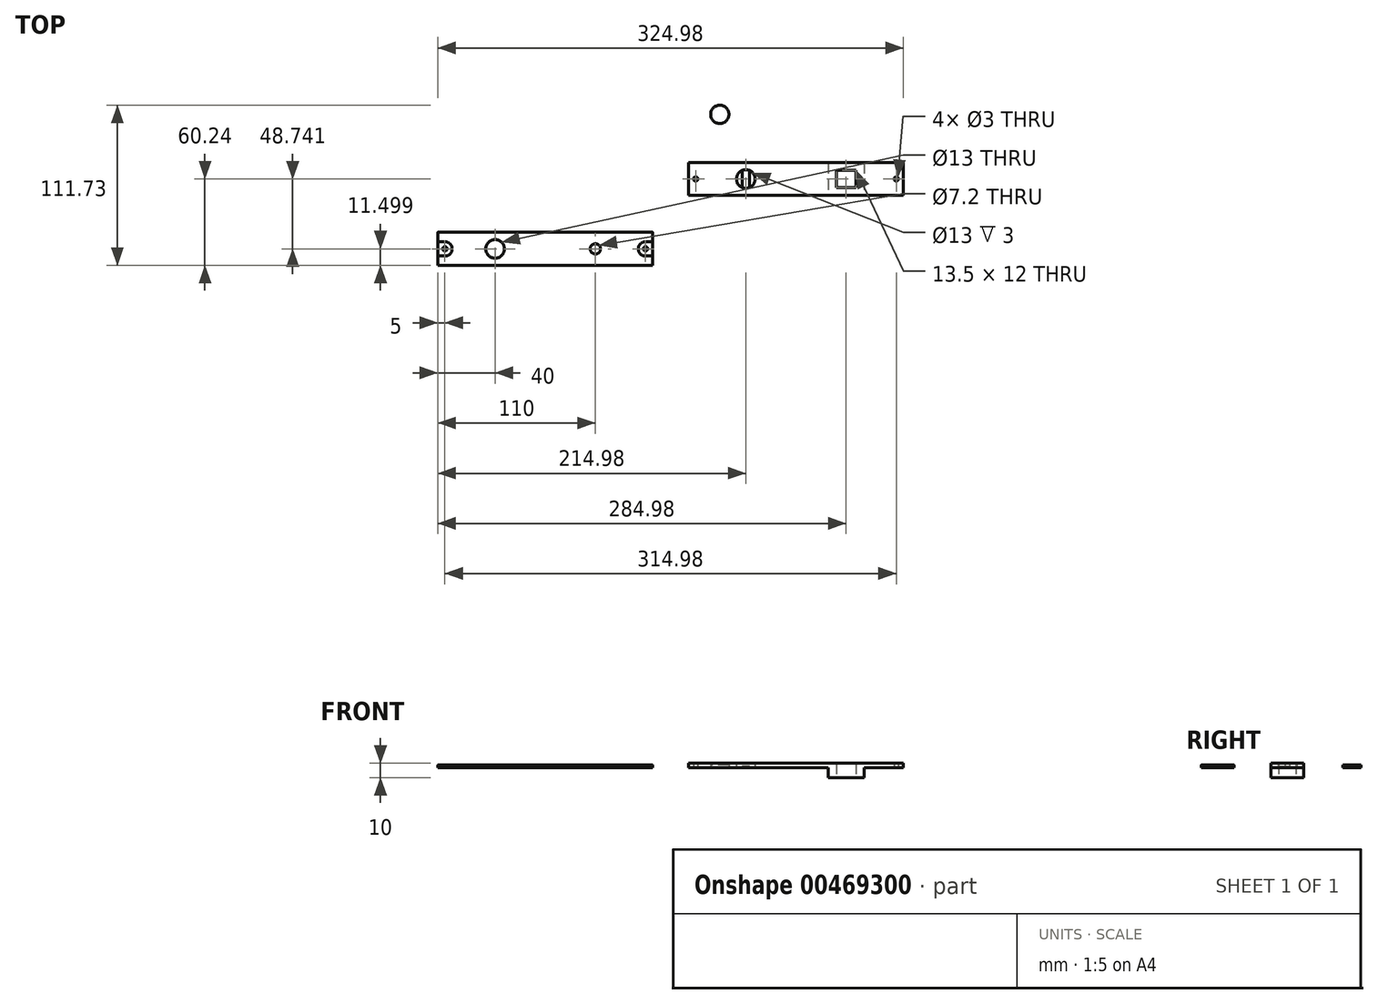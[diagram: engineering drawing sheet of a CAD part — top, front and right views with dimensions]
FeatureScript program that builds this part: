
annotation { "Feature Type Name" : "Feature", "Feature Type Description" : "" }
export const myFeature = defineFeature(function(context is Context, id is Id, definition is map)
    precondition{}
    {
        {
            var Q0;
            Q0=qCreatedBy(makeId("Top.planeOp"),FACE);
            var sketch = newSketch(context, id + "F0", { "sketchPlane" : qUnion([Q0])});
            skLineSegment(sketch, "E0.bottom", {"start": v(75, -11.5) * mm, "end": v(-75, -11.5) * mm});
            skLineSegment(sketch, "E0.top", {"start": v(75, 11.5) * mm, "end": v(-75, 11.5) * mm});
            skLineSegment(sketch, "E0.left", {"start": v(75, -11.5) * mm, "end": v(75, 11.5) * mm});
            skLineSegment(sketch, "E0.right", {"start": v(-75, -11.5) * mm, "end": v(-75, 11.5) * mm});
            skPoint(sketch, "E0.middle", {"position": v(0, 0) * mm});
            skCircle(sketch, "E1", {"center": v(-35, 0) * mm, "radius": 6.5 * mm});
            skLineSegment(sketch, "E2.bottom", {"start": v(-75, 11.5) * mm, "end": v(-65, 11.5) * mm, "construction": true});
            skLineSegment(sketch, "E2.top", {"start": v(-75, -11.5) * mm, "end": v(-65, -11.5) * mm, "construction": true});
            skLineSegment(sketch, "E2.left", {"start": v(-75, 11.5) * mm, "end": v(-75, -11.5) * mm, "construction": true});
            skLineSegment(sketch, "E2.right", {"start": v(-65, 11.5) * mm, "end": v(-65, -11.5) * mm, "construction": true});
            skLineSegment(sketch, "E3.bottom", {"start": v(75, -11.5) * mm, "end": v(65, -11.5) * mm, "construction": true});
            skLineSegment(sketch, "E3.top", {"start": v(75, 11.5) * mm, "end": v(65, 11.5) * mm, "construction": true});
            skLineSegment(sketch, "E3.left", {"start": v(75, -11.5) * mm, "end": v(75, 11.5) * mm, "construction": true});
            skLineSegment(sketch, "E3.right", {"start": v(65, -11.5) * mm, "end": v(65, 11.5) * mm, "construction": true});
            skLineSegment(sketch, "E4.bottom", {"start": v(41.75, -6) * mm, "end": v(28.25, -6) * mm});
            skLineSegment(sketch, "E4.top", {"start": v(41.75, 6) * mm, "end": v(28.25, 6) * mm});
            skLineSegment(sketch, "E4.left", {"start": v(41.75, -6) * mm, "end": v(41.75, 6) * mm});
            skLineSegment(sketch, "E4.right", {"start": v(28.25, -6) * mm, "end": v(28.25, 6) * mm});
            skPoint(sketch, "E4.middle", {"position": v(35, 0) * mm});
            skLineSegment(sketch, "E5.bottom", {"start": v(39, -6) * mm, "end": v(31, -6) * mm});
            skLineSegment(sketch, "E5.top", {"start": v(39, 6) * mm, "end": v(31, 6) * mm});
            skLineSegment(sketch, "E5.left", {"start": v(39, -6) * mm, "end": v(39, 6) * mm});
            skLineSegment(sketch, "E5.right", {"start": v(31, -6) * mm, "end": v(31, 6) * mm});
            skCircle(sketch, "E6", {"center": v(-70, 0) * mm, "radius": 1.5 * mm});
            skLineSegment(sketch, "E7.bottom", {"start": v(-65, 11.5) * mm, "end": v(-67, 11.5) * mm, "construction": true});
            skLineSegment(sketch, "E7.top", {"start": v(-65, -11.5) * mm, "end": v(-67, -11.5) * mm, "construction": true});
            skLineSegment(sketch, "E7.right", {"start": v(-67, 11.5) * mm, "end": v(-67, -11.5) * mm, "construction": true});
            skCircle(sketch, "E8", {"center": v(70, 0) * mm, "radius": 1.5 * mm});
            skLineSegment(sketch, "E9.bottom", {"start": v(-32.5, -6) * mm, "end": v(-37.5, -6) * mm, "construction": true});
            skLineSegment(sketch, "E9.top", {"start": v(-32.5, 6) * mm, "end": v(-37.5, 6) * mm, "construction": true});
            skLineSegment(sketch, "E9.left", {"start": v(-32.5, -6) * mm, "end": v(-32.5, 6) * mm});
            skLineSegment(sketch, "E9.right", {"start": v(-37.5, -6) * mm, "end": v(-37.5, 6) * mm});
            skSolve(sketch);
        }
        {
            var Q0;
            Q0=makeQuery(id+"F0.imprint","IMPRINT",FACE,{"disambiguationData":[TD([[makeQuery(id+"F0.imprint","IMPRINT",EDGE,{"derivedFrom":sQuery(id+"F0.wireOp",EDGE,"E0.bottom")}),-1.0]])]});
            var Q1;
            Q1=makeQuery(id+"F0.imprint","IMPRINT",FACE,{"disambiguationData":[TD([[makeQuery(id+"F0.imprint","IMPRINT",EDGE,{"derivedFrom":sQuery(id+"F0.wireOp",EDGE,"E5.bottom")}),-1.0]])]});
            var Q2;
            {var subQ0=sQuery(id+"F0.wireOp",EDGE,"E9.left");Q2=makeQuery(id+"F0.imprint","IMPRINT",FACE,{"disambiguationData":[TD([[makeQuery(id+"F0.imprint","IMPRINT",EDGE,{"derivedFrom":subQ0}),1.0]])]});}
            extrude(context, id + "F1", {"entities" : qUnion([Q0, Q1, Q2]), "depth" : 3 * mm});
        }
        {
            var Q0;
            Q0=qCreatedBy(makeId("Top.planeOp"),FACE);
            var sketch = newSketch(context, id + "F2", { "sketchPlane" : qUnion([Q0])});
            skLineSegment(sketch, "E10.bottom", {"start": v(-99.98, -60.24) * mm, "end": v(-249.98, -60.24) * mm});
            skLineSegment(sketch, "E10.top", {"start": v(-99.98, -37.24) * mm, "end": v(-249.98, -37.24) * mm});
            skLineSegment(sketch, "E10.left", {"start": v(-99.98, -60.24) * mm, "end": v(-99.98, -37.24) * mm});
            skLineSegment(sketch, "E10.right", {"start": v(-249.98, -60.24) * mm, "end": v(-249.98, -37.24) * mm});
            skPoint(sketch, "E10.middle", {"position": v(-174.98, -48.74) * mm});
            skCircle(sketch, "E11", {"center": v(-209.98, -48.74) * mm, "radius": 6.5 * mm});
            skLineSegment(sketch, "E12.bottom", {"start": v(-249.98, -37.24) * mm, "end": v(-239.98, -37.24) * mm, "construction": true});
            skLineSegment(sketch, "E12.top", {"start": v(-249.98, -60.24) * mm, "end": v(-239.98, -60.24) * mm, "construction": true});
            skLineSegment(sketch, "E12.left", {"start": v(-249.98, -37.24) * mm, "end": v(-249.98, -60.24) * mm, "construction": true});
            skLineSegment(sketch, "E12.right", {"start": v(-239.98, -37.24) * mm, "end": v(-239.98, -60.24) * mm, "construction": true});
            skLineSegment(sketch, "E13.bottom", {"start": v(-99.98, -60.24) * mm, "end": v(-109.98, -60.24) * mm, "construction": true});
            skLineSegment(sketch, "E13.top", {"start": v(-99.98, -37.24) * mm, "end": v(-109.98, -37.24) * mm, "construction": true});
            skLineSegment(sketch, "E13.left", {"start": v(-99.98, -60.24) * mm, "end": v(-99.98, -37.24) * mm, "construction": true});
            skLineSegment(sketch, "E13.right", {"start": v(-109.98, -60.24) * mm, "end": v(-109.98, -37.24) * mm, "construction": true});
            skLineSegment(sketch, "E14.bottom", {"start": v(-131.98, -55.74) * mm, "end": v(-147.98, -55.74) * mm, "construction": true});
            skLineSegment(sketch, "E14.top", {"start": v(-131.98, -41.74) * mm, "end": v(-147.98, -41.74) * mm, "construction": true});
            skLineSegment(sketch, "E14.left", {"start": v(-131.98, -55.74) * mm, "end": v(-131.98, -41.74) * mm, "construction": true});
            skLineSegment(sketch, "E14.right", {"start": v(-147.98, -55.74) * mm, "end": v(-147.98, -41.74) * mm, "construction": true});
            skPoint(sketch, "E14.middle", {"position": v(-139.98, -48.74) * mm});
            skLineSegment(sketch, "E15.bottom", {"start": v(-135.98, -55.74) * mm, "end": v(-143.98, -55.74) * mm});
            skLineSegment(sketch, "E15.top", {"start": v(-135.98, -41.74) * mm, "end": v(-143.98, -41.74) * mm});
            skLineSegment(sketch, "E15.left", {"start": v(-135.98, -55.74) * mm, "end": v(-135.98, -41.74) * mm, "construction": true});
            skLineSegment(sketch, "E15.right", {"start": v(-143.98, -55.74) * mm, "end": v(-143.98, -41.74) * mm, "construction": true});
            skCircle(sketch, "E16", {"center": v(-244.98, -48.74) * mm, "radius": 1.5 * mm});
            skCircle(sketch, "E17", {"center": v(-244.98, -55.24) * mm, "radius": 1.5 * mm, "construction": true});
            skCircle(sketch, "E18", {"center": v(-104.98, -48.74) * mm, "radius": 1.5 * mm});
            skCircle(sketch, "E19", {"center": v(-104.98, -55.24) * mm, "radius": 1.5 * mm, "construction": true});
            skCircle(sketch, "E20", {"center": v(-139.98, -48.74) * mm, "radius": 3.6 * mm});
            skLineSegment(sketch, "E21.bottom", {"start": v(-207.48, -54.74) * mm, "end": v(-212.48, -54.74) * mm, "construction": true});
            skLineSegment(sketch, "E21.top", {"start": v(-207.48, -42.74) * mm, "end": v(-212.48, -42.74) * mm, "construction": true});
            skLineSegment(sketch, "E21.left", {"start": v(-207.48, -54.74) * mm, "end": v(-207.48, -42.74) * mm});
            skLineSegment(sketch, "E21.right", {"start": v(-212.48, -54.74) * mm, "end": v(-212.48, -42.74) * mm});
            skSolve(sketch);
        }
        {
            var Q0;
            Q0=makeQuery(id+"F2.imprint","IMPRINT",FACE,{"disambiguationData":[TD([[makeQuery(id+"F2.imprint","IMPRINT",EDGE,{"derivedFrom":sQuery(id+"F2.wireOp",EDGE,"E10.bottom")}),-1.0]])]});
            extrude(context, id + "F3", {"entities" : qUnion([Q0]), "depth" : 2 * mm});
        }
        {
            var Q0;
            Q0=makeQuery(id+"F1.opExtrude","CAP_FACE",FACE,{"disambiguationData":[OSD([sQuery(id+"F0.wireOp",EDGE,"E0.bottom"),sQuery(id+"F0.wireOp",EDGE,"E0.top"),sQuery(id+"F0.wireOp",EDGE,"E0.left"),sQuery(id+"F0.wireOp",EDGE,"E0.right"),sQuery(id+"F0.wireOp",EDGE,"E1"),sQuery(id+"F0.wireOp",EDGE,"E4.bottom"),sQuery(id+"F0.wireOp",EDGE,"E4.top"),sQuery(id+"F0.wireOp",EDGE,"E4.left"),sQuery(id+"F0.wireOp",EDGE,"E4.right"),sQuery(id+"F0.wireOp",EDGE,"E5.left"),sQuery(id+"F0.wireOp",EDGE,"E5.right")])],"isStart":true});
            var sketch = newSketch(context, id + "F4", { "sketchPlane" : qUnion([Q0])});
            skPoint(sketch, "E22.0", {"position": v(35, 0) * mm});
            skLineSegment(sketch, "E23.bottom", {"start": v(47.5, -11.5) * mm, "end": v(22.5, -11.5) * mm});
            skLineSegment(sketch, "E23.top", {"start": v(47.5, 11.5) * mm, "end": v(22.5, 11.5) * mm});
            skLineSegment(sketch, "E23.left", {"start": v(47.5, -11.5) * mm, "end": v(47.5, 11.5) * mm});
            skLineSegment(sketch, "E23.right", {"start": v(22.5, -11.5) * mm, "end": v(22.5, 11.5) * mm});
            skLineSegment(sketch, "E24.bottom", {"start": v(41.75, -6) * mm, "end": v(28.25, -6) * mm});
            skLineSegment(sketch, "E24.top", {"start": v(41.75, 6) * mm, "end": v(28.25, 6) * mm});
            skLineSegment(sketch, "E24.left", {"start": v(41.75, -6) * mm, "end": v(41.75, 6) * mm});
            skLineSegment(sketch, "E24.right", {"start": v(28.25, -6) * mm, "end": v(28.25, 6) * mm});
            skLineSegment(sketch, "E25.bottom", {"start": v(39, -6) * mm, "end": v(31, -6) * mm});
            skLineSegment(sketch, "E25.top", {"start": v(39, 6) * mm, "end": v(31, 6) * mm});
            skLineSegment(sketch, "E25.left", {"start": v(39, -6) * mm, "end": v(39, 6) * mm});
            skLineSegment(sketch, "E25.right", {"start": v(31, -6) * mm, "end": v(31, 6) * mm});
            skSolve(sketch);
        }
        {
            var Q0;
            Q0 = qSketchRegion(id + "F4", true);
            var Q1;
            Q1=makeQuery(id+"F0.imprint","IMPRINT",FACE,{"disambiguationData":[TD([[makeQuery(id+"F0.imprint","IMPRINT",EDGE,{"derivedFrom":sQuery(id+"F0.wireOp",EDGE,"E5.bottom")}),-1.0]])]});
            extrude(context, id + "F5", {"entities" : qUnion([Q0, Q1]), "operationType" : NewBodyOperationType.ADD, "depth" : 7 * mm});
        }
        {
            var Q0;
            Q0=makeQuery(id+"F1.opExtrude","CAP_FACE",FACE,{"disambiguationData":[OSD([sQuery(id+"F0.wireOp",EDGE,"E0.bottom"),sQuery(id+"F0.wireOp",EDGE,"E0.top"),sQuery(id+"F0.wireOp",EDGE,"E0.left"),sQuery(id+"F0.wireOp",EDGE,"E0.right"),sQuery(id+"F0.wireOp",EDGE,"E1"),sQuery(id+"F0.wireOp",EDGE,"E4.bottom"),sQuery(id+"F0.wireOp",EDGE,"E4.top"),sQuery(id+"F0.wireOp",EDGE,"E4.left"),sQuery(id+"F0.wireOp",EDGE,"E4.right"),sQuery(id+"F0.wireOp",EDGE,"E5.left"),sQuery(id+"F0.wireOp",EDGE,"E5.right")])],"isStart":false});
            var sketch = newSketch(context, id + "F6", { "sketchPlane" : qUnion([Q0])});
            skPoint(sketch, "E26.0", {"position": v(35, 0) * mm});
            skLineSegment(sketch, "E27.bottom", {"start": v(41.75, -6) * mm, "end": v(28.25, -6) * mm});
            skLineSegment(sketch, "E27.top", {"start": v(41.75, 6) * mm, "end": v(28.25, 6) * mm});
            skLineSegment(sketch, "E27.left", {"start": v(41.75, -6) * mm, "end": v(41.75, 6) * mm});
            skLineSegment(sketch, "E27.right", {"start": v(28.25, -6) * mm, "end": v(28.25, 6) * mm});
            skSolve(sketch);
        }
        {
            var Q0;
            Q0 = qSketchRegion(id + "F6", true);
            extrude(context, id + "F7", {"entities" : qUnion([Q0]), "operationType" : NewBodyOperationType.REMOVE, "oppositeDirection" : true, "depth" : 9 * mm});
        }
        {
            var Q0;
            Q0=makeQuery(id+"F1.opExtrude","CAP_FACE",FACE,{"disambiguationData":[OSD([sQuery(id+"F0.wireOp",EDGE,"E0.bottom"),sQuery(id+"F0.wireOp",EDGE,"E0.top"),sQuery(id+"F0.wireOp",EDGE,"E0.left"),sQuery(id+"F0.wireOp",EDGE,"E0.right"),sQuery(id+"F0.wireOp",EDGE,"E1"),sQuery(id+"F0.wireOp",EDGE,"E4.bottom"),sQuery(id+"F0.wireOp",EDGE,"E4.top"),sQuery(id+"F0.wireOp",EDGE,"E4.left"),sQuery(id+"F0.wireOp",EDGE,"E4.right"),sQuery(id+"F0.wireOp",EDGE,"E5.left"),sQuery(id+"F0.wireOp",EDGE,"E5.right"),sQuery(id+"F0.wireOp",EDGE,"E6"),sQuery(id+"F0.wireOp",EDGE,"uwKOgWHx-wiQu-w8Me-ZzSO-K48oh4q2hqjQ"),sQuery(id+"F0.wireOp",EDGE,"E8"),sQuery(id+"F0.wireOp",EDGE,"GEiIiJwR-kFnx-osnd-0Qsu-TudxTzi2J8hG"),sQuery(id+"F0.wireOp",EDGE,"E9.left"),sQuery(id+"F0.wireOp",EDGE,"E9.right")])],"isStart":false});
            var sketch = newSketch(context, id + "F8", { "sketchPlane" : qUnion([Q0])});
            skPoint(sketch, "E28.0", {"position": v(-35, 0) * mm});
            skCircle(sketch, "E29", {"center": v(-35, 0) * mm, "radius": 6.5 * mm});
            skSolve(sketch);
        }
        {
            var Q0;
            Q0 = qSketchRegion(id + "F8", true);
            extrude(context, id + "F9", {"entities" : qUnion([Q0]), "operationType" : NewBodyOperationType.REMOVE, "oppositeDirection" : true, "depth" : 2 * mm});
        }
        {
            var Q0;
            Q0=qCreatedBy(makeId("Top.planeOp"),FACE);
            var sketch = newSketch(context, id + "F10", { "sketchPlane" : qUnion([Q0])});
            skCircle(sketch, "E30", {"center": v(-53.16, 45.1) * mm, "radius": 6.4 * mm});
            skSolve(sketch);
        }
        {
            var Q0;
            Q0=makeQuery(id+"F10.imprint","IMPRINT",FACE,{"disambiguationData":[TD([[makeQuery(id+"F10.imprint","IMPRINT",EDGE,{"derivedFrom":sQuery(id+"F10.wireOp",EDGE,"E30")}),1.0]])]});
            extrude(context, id + "F11", {"entities" : qUnion([Q0]), "depth" : 2 * mm});
        }
        {
            var Q0;
            Q0=makeQuery(id+"F3.opExtrude","CAP_FACE",FACE,{"disambiguationData":[OSD([sQuery(id+"F2.wireOp",EDGE,"E10.bottom"),sQuery(id+"F2.wireOp",EDGE,"E10.top"),sQuery(id+"F2.wireOp",EDGE,"E10.left"),sQuery(id+"F2.wireOp",EDGE,"E10.right"),sQuery(id+"F2.wireOp",EDGE,"E11"),sQuery(id+"F2.wireOp",EDGE,"E16"),sQuery(id+"F2.wireOp",EDGE,"E17"),sQuery(id+"F2.wireOp",EDGE,"E18"),sQuery(id+"F2.wireOp",EDGE,"E19"),sQuery(id+"F2.wireOp",EDGE,"E20")])],"isStart":false});
            var sketch = newSketch(context, id + "F12", { "sketchPlane" : qUnion([Q0])});
            skCircle(sketch, "E31", {"center": v(-244.98, -48.74) * mm, "radius": 5 * mm});
            skCircle(sketch, "E32", {"center": v(-104.98, -48.74) * mm, "radius": 5 * mm});
            skLineSegment(sketch, "E33.bottom", {"start": v(-244.98, -53.74) * mm, "end": v(-252.48, -53.74) * mm});
            skLineSegment(sketch, "E33.top", {"start": v(-244.98, -43.74) * mm, "end": v(-252.48, -43.74) * mm});
            skLineSegment(sketch, "E33.right", {"start": v(-252.48, -53.74) * mm, "end": v(-252.48, -43.74) * mm});
            skLineSegment(sketch, "E34.bottom", {"start": v(-97.48, -53.74) * mm, "end": v(-104.98, -53.74) * mm});
            skLineSegment(sketch, "E34.top", {"start": v(-97.48, -43.74) * mm, "end": v(-104.98, -43.74) * mm});
            skLineSegment(sketch, "E34.left", {"start": v(-97.48, -53.74) * mm, "end": v(-97.48, -43.74) * mm});
            skSolve(sketch);
        }
        {
            var Q0;
            Q0 = qSketchRegion(id + "F12", true);
            extrude(context, id + "F13", {"entities" : qUnion([Q0]), "operationType" : NewBodyOperationType.REMOVE, "oppositeDirection" : true, "depth" : 1 * mm});
        }
        {
            var Q0;
            Q0=makeQuery(id+"F3.opExtrude","CAP_EDGE",EDGE,{"disambiguationData":[OSD([sQuery(id+"F2.wireOp",EDGE,"E10.top")])],"isStart":false});
            var Q1;
            {var subQ0=sQuery(id+"F2.wireOp",EDGE,"E10.right");var subQ1=sQuery(id+"F2.wireOp",EDGE,"E10.top");Q1=makeQuery(id+"F13.boolean.opBoolean","SPLIT",EDGE,{"disambiguationData":[TD([makeQuery(id+"F3.opExtrude","SWEPT_FACE",FACE,{"disambiguationData":[OSD([subQ1])]})])],"derivedFrom":makeQuery(id+"F3.opExtrude","CAP_EDGE",EDGE,{"disambiguationData":[OSD([subQ0])],"isStart":false})});}
            var Q2;
            Q2=makeQuery(id+"F13.boolean.opBoolean","COPY",EDGE,{"derivedFrom":makeQuery(id+"F13.opExtrude","CAP_EDGE",EDGE,{"disambiguationData":[OSD([sQuery(id+"F12.wireOp",EDGE,"E33.top")])],"isStart":true})});
            var Q3;
            {var subQ0=sQuery(id+"F2.wireOp",EDGE,"E10.bottom");var subQ1=sQuery(id+"F2.wireOp",EDGE,"E10.right");Q3=makeQuery(id+"F13.boolean.opBoolean","SPLIT",EDGE,{"disambiguationData":[TD([makeQuery(id+"F3.opExtrude","SWEPT_FACE",FACE,{"disambiguationData":[OSD([subQ0])]})])],"derivedFrom":makeQuery(id+"F3.opExtrude","CAP_EDGE",EDGE,{"disambiguationData":[OSD([subQ1])],"isStart":false})});}
            var Q4;
            Q4=makeQuery(id+"F3.opExtrude","CAP_EDGE",EDGE,{"disambiguationData":[OSD([sQuery(id+"F2.wireOp",EDGE,"E10.bottom")])],"isStart":false});
            var Q5;
            {var subQ0=sQuery(id+"F2.wireOp",EDGE,"E10.bottom");var subQ1=sQuery(id+"F2.wireOp",EDGE,"E10.left");Q5=makeQuery(id+"F13.boolean.opBoolean","SPLIT",EDGE,{"disambiguationData":[TD([makeQuery(id+"F3.opExtrude","SWEPT_FACE",FACE,{"disambiguationData":[OSD([subQ0])]})])],"derivedFrom":makeQuery(id+"F3.opExtrude","CAP_EDGE",EDGE,{"disambiguationData":[OSD([subQ1])],"isStart":false})});}
            var Q6;
            Q6=makeQuery(id+"F13.boolean.opBoolean","COPY",EDGE,{"derivedFrom":makeQuery(id+"F13.opExtrude","CAP_EDGE",EDGE,{"disambiguationData":[OSD([sQuery(id+"F12.wireOp",EDGE,"E34.bottom")])],"isStart":true})});
            var Q7;
            {var subQ0=sQuery(id+"F2.wireOp",EDGE,"E10.left");var subQ1=sQuery(id+"F2.wireOp",EDGE,"E10.top");Q7=makeQuery(id+"F13.boolean.opBoolean","SPLIT",EDGE,{"disambiguationData":[TD([makeQuery(id+"F3.opExtrude","SWEPT_FACE",FACE,{"disambiguationData":[OSD([subQ1])]})])],"derivedFrom":makeQuery(id+"F3.opExtrude","CAP_EDGE",EDGE,{"disambiguationData":[OSD([subQ0])],"isStart":false})});}
            fillet(context, id + "F14", {"entities" : qUnion([Q0, Q1, Q2, Q3, Q4, Q5, Q6, Q7]), "radius" : 0.5 * mm, "tangentPropagation" : true, "allowEdgeOverflow" : false});
        }
    });
